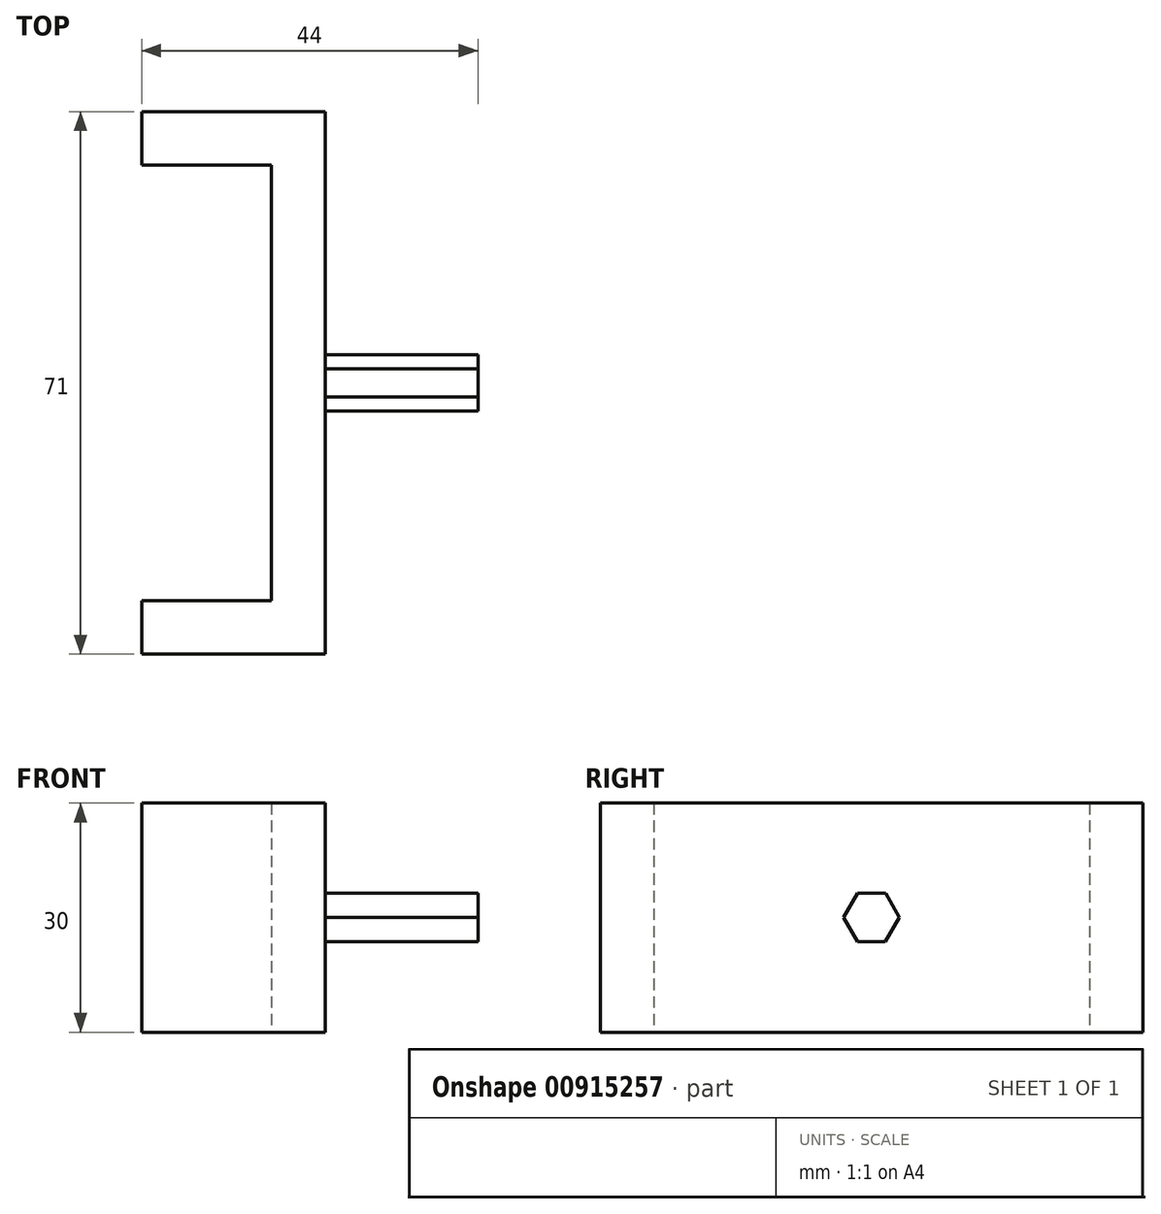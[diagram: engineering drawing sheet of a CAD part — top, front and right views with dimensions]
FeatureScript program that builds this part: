
annotation { "Feature Type Name" : "Feature", "Feature Type Description" : "" }
export const myFeature = defineFeature(function(context is Context, id is Id, definition is map)
    precondition{}
    {
        {
            var Q0;
            Q0=qCreatedBy(makeId("Top.planeOp"),FACE);
            var sketch = newSketch(context, id + "F0", { "sketchPlane" : qUnion([Q0])});
            skLineSegment(sketch, "E0.bottom", {"start": v(0, 38.48) * mm, "end": v(7, 38.48) * mm});
            skLineSegment(sketch, "E0.left", {"start": v(0, 38.48) * mm, "end": v(0, -18.52) * mm});
            skLineSegment(sketch, "E0.right", {"start": v(7, 38.48) * mm, "end": v(7, -18.52) * mm});
            skLineSegment(sketch, "E1.bottom", {"start": v(0, 38.48) * mm, "end": v(-17, 38.48) * mm});
            skLineSegment(sketch, "E1.top", {"start": v(0, 45.48) * mm, "end": v(-17, 45.48) * mm});
            skLineSegment(sketch, "E1.left", {"start": v(0, 38.48) * mm, "end": v(0, 45.48) * mm});
            skLineSegment(sketch, "E1.right", {"start": v(-17, 38.48) * mm, "end": v(-17, 45.48) * mm});
            skLineSegment(sketch, "E2.bottom", {"start": v(0, 45.48) * mm, "end": v(7, 45.48) * mm});
            skLineSegment(sketch, "E2.left", {"start": v(0, 45.48) * mm, "end": v(0, 38.48) * mm});
            skLineSegment(sketch, "E2.right", {"start": v(7, 45.48) * mm, "end": v(7, 38.48) * mm});
            skLineSegment(sketch, "E3.bottom", {"start": v(7, -18.52) * mm, "end": v(-17, -18.52) * mm});
            skLineSegment(sketch, "E3.top", {"start": v(7, -25.52) * mm, "end": v(-17, -25.52) * mm});
            skLineSegment(sketch, "E3.left", {"start": v(7, -18.52) * mm, "end": v(7, -25.52) * mm});
            skLineSegment(sketch, "E3.right", {"start": v(-17, -18.52) * mm, "end": v(-17, -25.52) * mm});
            skSolve(sketch);
        }
        {
            var Q0;
            Q0=makeQuery(id+"F0.imprint","IMPRINT",FACE,{"disambiguationData":[TD([[makeQuery(id+"F0.imprint","IMPRINT",EDGE,{"derivedFrom":sQuery(id+"F0.wireOp",EDGE,"E1.bottom")}),-1.0]])]});
            var Q1;
            Q1=makeQuery(id+"F0.imprint","IMPRINT",FACE,{"disambiguationData":[TD([[makeQuery(id+"F0.imprint","IMPRINT",EDGE,{"derivedFrom":sQuery(id+"F0.wireOp",EDGE,"E2.bottom")}),-1.0]])]});
            var Q2;
            {var subQ0=sQuery(id+"F0.wireOp",EDGE,"E0.left");Q2=makeQuery(id+"F0.imprint","IMPRINT",FACE,{"disambiguationData":[TD([[makeQuery(id+"F0.imprint","IMPRINT",EDGE,{"derivedFrom":subQ0}),1.0]])]});}
            var Q3;
            Q3=makeQuery(id+"F0.imprint","IMPRINT",FACE,{"disambiguationData":[TD([[makeQuery(id+"F0.imprint","IMPRINT",EDGE,{"derivedFrom":sQuery(id+"F0.wireOp",EDGE,"E3.top")}),-1.0]])]});
            extrude(context, id + "F1", {"entities" : qUnion([Q0, Q1, Q2, Q3]), "depth" : 30 * mm, "offsetDistance" : 25 * mm});
        }
        {
            var Q0;
            Q0=makeQuery(id+"F1.opExtrude","SWEPT_FACE",FACE,{"disambiguationData":[OSD([sQuery(id+"F0.wireOp",EDGE,"E0.right"),sQuery(id+"F0.wireOp",EDGE,"E2.right"),sQuery(id+"F0.wireOp",EDGE,"E3.left")])]});
            var sketch = newSketch(context, id + "F2", { "sketchPlane" : qUnion([Q0])});
            skCircle(sketch, "E4.cCircle", {"center": v(9.98, 15) * mm, "radius": 3.17 * mm, "construction": true});
            skLineSegment(sketch, "E4.0", {"start": v(6.32, 15) * mm, "end": v(8.15, 18.18) * mm});
            skLineSegment(sketch, "E4.1", {"start": v(8.15, 18.18) * mm, "end": v(11.82, 18.17) * mm});
            skLineSegment(sketch, "E4.2", {"start": v(11.82, 18.17) * mm, "end": v(13.65, 15) * mm});
            skLineSegment(sketch, "E4.3", {"start": v(13.65, 15) * mm, "end": v(11.82, 11.82) * mm});
            skLineSegment(sketch, "E4.4", {"start": v(11.82, 11.82) * mm, "end": v(8.15, 11.83) * mm});
            skLineSegment(sketch, "E4.5", {"start": v(8.15, 11.83) * mm, "end": v(6.32, 15) * mm});
            skPoint(sketch, "E4.0.midPoint", {"position": v(7.23, 16.59) * mm});
            skSolve(sketch);
        }
        {
            var Q0;
            Q0=makeQuery(id+"F2.imprint","IMPRINT",FACE,{"disambiguationData":[TD([[makeQuery(id+"F2.imprint","IMPRINT",EDGE,{"derivedFrom":sQuery(id+"F2.wireOp",EDGE,"E4.0")}),-1.0]])]});
            extrude(context, id + "F3", {"entities" : qUnion([Q0]), "operationType" : NewBodyOperationType.ADD, "depth" : 20 * mm, "offsetDistance" : 25 * mm});
        }
    });
